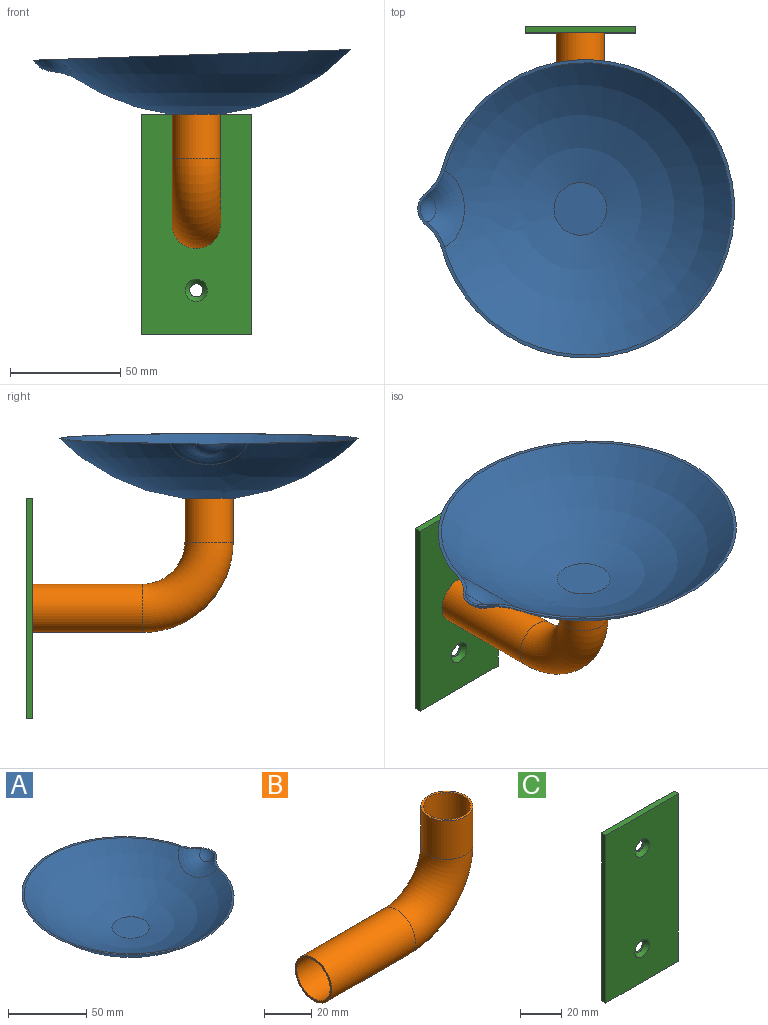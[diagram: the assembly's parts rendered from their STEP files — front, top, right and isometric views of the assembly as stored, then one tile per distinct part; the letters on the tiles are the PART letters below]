
ASSEMBLY  parts=3 mates=2
PART A: 9 faces, bbox 143.8x140x29.9 mm
  f0: plane 143.78x135.48mm, normal (0.03,0,1), area 607.5mm2, adj f1,f2,f3,f5,f6,f7
  f1: sphere r=96.67mm, area 15967.4mm2, adj f0,f3,f4
  f2: sphere r=10mm, area 110.5mm2, adj f0,f3
  f3: torus R=23.03mm, axis (-0.7,0,0.72), area 445.1mm2, adj f0,f1,f2
  f4: plane 24x24mm, normal (0,0,-1), area 452.4mm2, adj f1
  f5: sphere r=95.67mm, area 15241.4mm2, adj f0,f7,f8
  f6: sphere r=9mm, area 82.7mm2, adj f0,f7
  f7: torus R=23.03mm, axis (-0.7,0,0.72), area 420.1mm2, adj f0,f5,f6
  f8: plane 23.88x23.88mm, normal (0,0,1), area 447.7mm2, adj f5
PART B: 8 faces, bbox 94.4x22x64.4 mm
  f0: cylinder r=10mm len=50mm, axis (1,0,0), area 3141.6mm2, adj f1,f3
  f1: torus R=30mm, axis (0,-1,0), area 2960.9mm2, adj f0,f2
  f2: cylinder r=10mm len=20mm, axis (0,0,1), area 1256.6mm2, adj f1,f4
  f3: plane 22x22mm, normal (-1,0,0), area 66mm2, adj f0,f5
  f4: plane 22x22mm, normal (0,0,1), area 66mm2, adj f2,f7
  f5: cylinder r=11mm len=50mm, axis (1,0,0), area 3455.8mm2, adj f3,f6
  f6: torus R=30mm, axis (0,-1,0), area 3257mm2, adj f5,f7
  f7: cylinder r=11mm len=22mm, axis (0,0,1), area 1382.3mm2, adj f4,f6
PART C: 10 faces, bbox 50x3x100 mm
  f0: plane 50x3mm, normal (0,0,-1), area 150mm2, adj f1,f3,f4,f5
  f1: plane 100x3mm, normal (1,0,0), area 300mm2, adj f0,f2,f4,f5
  f2: plane 50x3mm, normal (0,0,1), area 150mm2, adj f1,f3,f4,f5
  f3: plane 100x3mm, normal (-1,0,0), area 300mm2, adj f0,f2,f4,f5
  f4: plane 100x50mm, normal (0,1,0), area 4943.5mm2, adj f0,f1,f2,f3,f6,f8
  f5: plane 100x50mm, normal (0,-1,0), area 4842.9mm2, adj f0,f1,f2,f3,f7,f9
  f6: cylinder r=3mm len=6mm, axis (0,-1,0), area 18.8mm2, adj f4,f7
  f7: cone r=3mm half-angle=45deg, axis (0,-1,0), area 71.1mm2, adj f5,f6
  f8: cylinder r=3mm len=6mm, axis (0,-1,0), area 18.8mm2, adj f4,f9
  f9: cone r=3mm half-angle=45deg, axis (0,-1,0), area 71.1mm2, adj f5,f8
PLACE A rot(axis=(0,0,-1),180deg) t=(-64.13,-37.6,-16.24)mm
PLACE B rot(axis=(0,0,-1),90deg) t=(-64.13,-37.6,-65.49)mm
PLACE C t=(-64.13,42.4,-65.49)mm
MATE fastened A.f4 <-> B.f2  axis (0,0,-1) through (-64.13,-37.6,-15.49)mm
MATE fastened B.f0 <-> C.f5  axis (0,-1,0) through (-64.13,42.4,-65.49)mm
